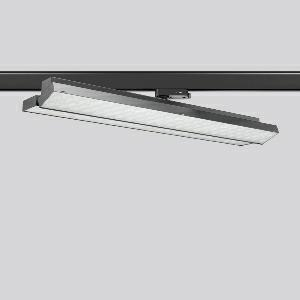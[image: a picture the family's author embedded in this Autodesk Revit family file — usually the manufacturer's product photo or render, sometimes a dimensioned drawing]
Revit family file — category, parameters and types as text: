
# Revit family: tx-move_742161_003_1_76_9b42
name_source: partatom
category: Lighting Fixtures
units: mm (PartAtom-declared; Revit-internal decimal feet)

## family parameters
Cut with Voids When Loaded = No
Host = Face
Light Source = No
Part Type = Normal
Room Calculation Point = No
Round Connector Dimension = Use Diameter
Shared = No

## types (1)
- MultiLumen 1 (1 x LED Modul 840, 3125 lm, 4000)
    Apparent Load = 41 VA
    CIE Flux Codes = 90 97 99 100 100
    Color Rendering = 80
    Color Temperature = 4000
    Default Elevation = 1800 mm
    Description = Series: TX-MOVE
Multifunctional surface-mounted spotlight for area lighting. Very flat design. Housing: sheet steel, powder-coated. Rotation range: 356°. Swivel range: 90°. Consistent alignment possible with visible tilt scale. High-efficiency LED units with optimum light control thanks to clear plastic (PC) lens optics. Spezielle Mikrostrukturen reduzieren Gelbsaum. Symmetrical light distribution. With adapter for RZB 3-circuit DALI tracks. Suitable for Track on ceiling. MultiLumen: Luminous flux adjustable in 3 steps. Factory setting is the highest luminous flux. Environmentally friendly and resource-saving due to replaceable and recyclable components. Very good glare control, ideal for till areas. 
Colour: deep black, matt (RAL 9005)
Length: 570 mm
Width: 119 mm
Height: 88 mm
Lamp: LED
Socket: without socket
Colour temperature: 4000K
Colour rendering index (CRI): 80
System power: 41 W
Rated luminous flux: 6250 lm
Luminous efficiency: 152 lm/W
System power 2: 57 W
Rated luminous flux 2: 8450 lm
Luminous efficiency 2: 148 lm/W
System power 3: 73 W
Rated luminous flux 3: 10400 lm
Luminous efficiency 3: 142 lm/W
Control gear: Dimmable EVG, DALI
Protection class: I
Type of protection: IP 20
    Height = 75 mm
    Lamp = 1 x LED Modul 840
    Lamp Light Flux = 3125 lm
    Lamp count = 1
    Length = 569 mm
    Lifetime = 50000 h
    Luminous efficacy = 152 lm/W
    Manufacturer = RZB
    ModVariant = No
    Model = 742161.003.1.76
    Mounting Place = Ceiling
    Mounting Type = Surface mounted
    Number of Poles = 1
    OnlyDefault = Yes
    Power Factor = 1
    Product Name = TX-MOVE
    Product group = Track mounted projectors
    ProductGroupID = 301
    Protection Class = Protection class I
    Protection Degree = IP 20
    RLX_Detail_Level = 1
    RLX_Emergency_Light_Flux = 0 lm
    RLX_Emergency_Type = 0
    RLX_Emergency_Type_DB = No
    RlxData = <blob elided: 36893 chars, md5=3eb76b88>
    Socket = socket
    Standby Power = 0 W
    System Light Flux = 6250 lm
    System Power = 41 W
    Type Comments = MultiLumen 1
    Type Image = 742162.003.jpg
    URL = http://relux.com
    VarID = multilumen_1
    Voltage = 0 V
    Weight = 0.00 kg
    Width = 119 mm

## geometry (parser evidence)
native form markers: Blend x4, Sweep x15
no freeform markers — native parametric forms only
